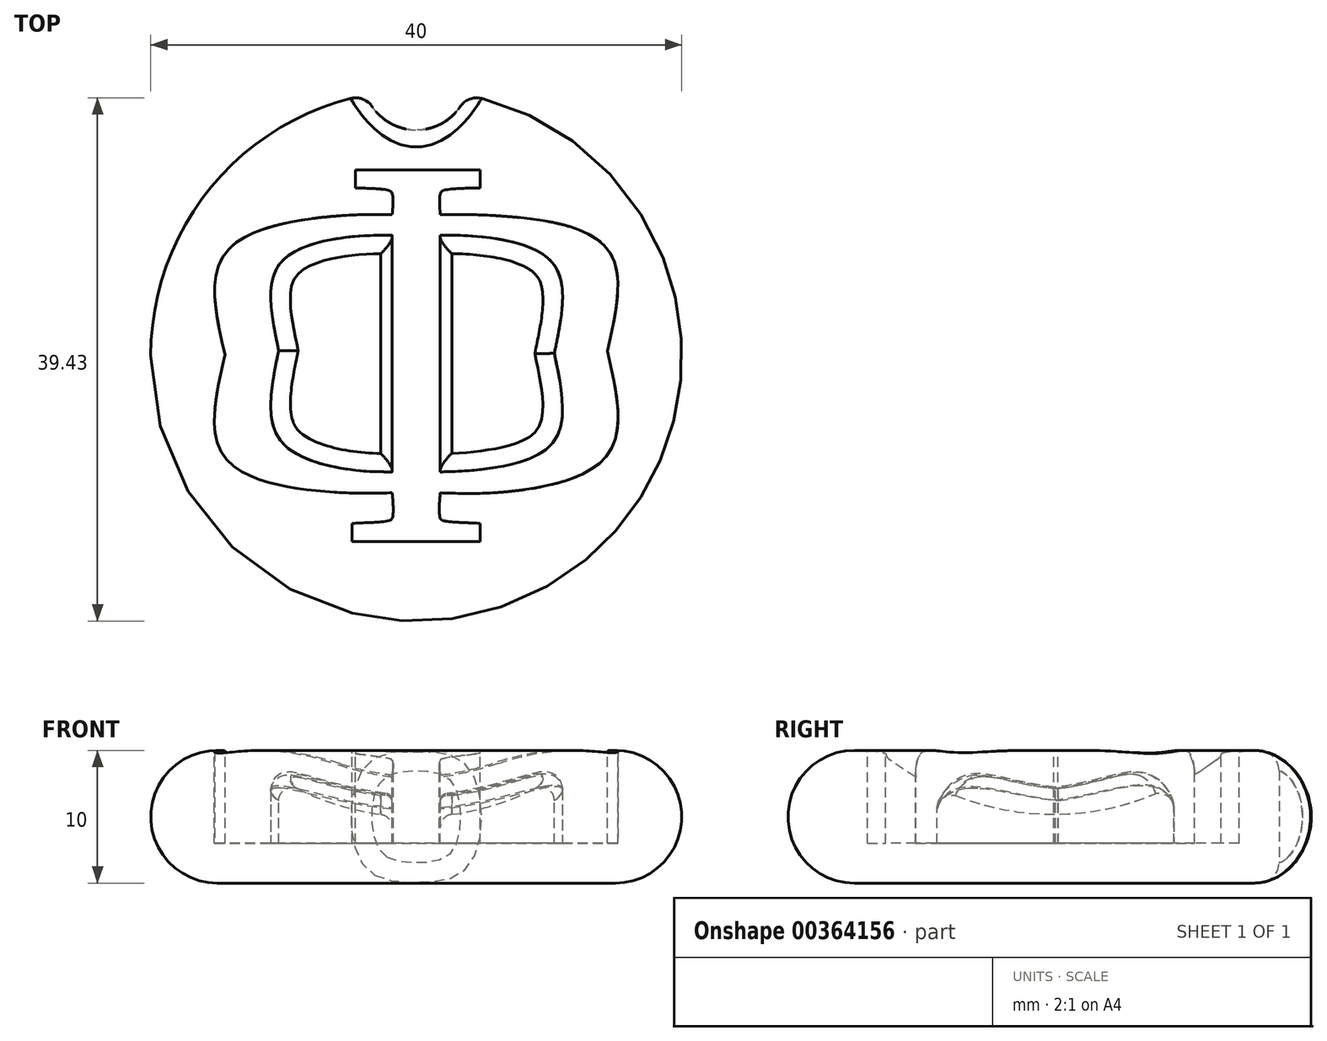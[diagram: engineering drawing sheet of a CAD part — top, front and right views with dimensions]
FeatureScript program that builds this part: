
annotation { "Feature Type Name" : "Feature", "Feature Type Description" : "" }
export const myFeature = defineFeature(function(context is Context, id is Id, definition is map)
    precondition{}
    {
        {
            var Q0;
            Q0=qCreatedBy(makeId("Right.planeOp"),FACE);
            var sketch = newSketch(context, id + "F0", { "sketchPlane" : qUnion([Q0])});
            skArc(sketch, "E0", {"start": v(-12, 9) * mm, "mid": v(-19.74, 6.58) * mm, "end": v(-15, 0) * mm});
            skArc(sketch, "E1", {"start": v(-12, 9) * mm, "mid": v(-6.32, 6.03) * mm, "end": v(0, 5) * mm});
            skLineSegment(sketch, "E2", {"start": v(-15, 0) * mm, "end": v(0, 0) * mm});
            skLineSegment(sketch, "E3", {"start": v(0, 0) * mm, "end": v(0, 5) * mm});
            skSolve(sketch);
        }
        {
            var Q0;
            Q0=makeQuery(id+"F0.imprint","IMPRINT",FACE,{"disambiguationData":[TD([[makeQuery(id+"F0.imprint","IMPRINT",EDGE,{"derivedFrom":sQuery(id+"F0.wireOp",EDGE,"E0")}),1.0]])]});
            var Q1;
            Q1=sQuery(id+"F0.wireOp",EDGE,"E3");
            revolve(context, id + "F1", {"entities" : qUnion([Q0]), "axis" : qUnion([Q1]), "revolveType" : RevolveType.FULL});
        }
        {
            var Q0;
            Q0=qCreatedBy(makeId("Top.planeOp"),FACE);
            cPlane(context, id + "F2", {"entities" : qUnion([Q0]), "cplaneType" : CPlaneType.OFFSET, "offset" : 25 * mm, "width" : 150 * mm, "height" : 150 * mm});
        }
        {
            var Q0;
            Q0=qCreatedBy(id+"F2.planeOp",FACE);
            var sketch = newSketch(context, id + "F3", { "sketchPlane" : qUnion([Q0])});
            skFitSpline(sketch, "E4", {"points": [v(4.83, 12.64) * mm, v(2.1, 12.47) * mm, v(1.8, 12.21) * mm, v(1.8, 10.64) * mm]});
            skFitSpline(sketch, "E5", {"points": [v(1.8, 10.64) * mm, v(7.04, 10.47) * mm, v(14.4, 8.04) * mm, v(14.4, 0.34) * mm]});
            skFitSpline(sketch, "E6", {"points": [v(14.4, 0.34) * mm, v(14.4, -7.49) * mm, v(6.87, -10.26) * mm, v(1.8, -10.34) * mm]});
            skFitSpline(sketch, "E7", {"points": [v(1.8, -10.34) * mm, v(1.8, -12.26) * mm, v(2.15, -12.47) * mm, v(4.83, -12.64) * mm]});
            skFitSpline(sketch, "E8", {"points": [v(-4.83, -12.64) * mm, v(-2.15, -12.47) * mm, v(-1.8, -12.26) * mm, v(-1.8, -10.34) * mm]});
            skFitSpline(sketch, "E9", {"points": [v(-1.8, -10.34) * mm, v(-6.74, -10.26) * mm, v(-14.4, -7.7) * mm, v(-14.4, 0.04) * mm]});
            skFitSpline(sketch, "E10", {"points": [v(-14.4, 0.04) * mm, v(-14.4, 7.7) * mm, v(-7, 10.43) * mm, v(-1.8, 10.64) * mm]});
            skFitSpline(sketch, "E11", {"points": [v(-1.8, 10.64) * mm, v(-1.8, 12.21) * mm, v(-2.15, 12.47) * mm, v(-4.57, 12.64) * mm]});
            skLineSegment(sketch, "E12", {"start": v(4.83, -12.64) * mm, "end": v(4.83, -14) * mm});
            skLineSegment(sketch, "E13", {"start": v(4.83, -14) * mm, "end": v(-4.83, -14) * mm});
            skLineSegment(sketch, "E14", {"start": v(-4.83, -14) * mm, "end": v(-4.83, -12.64) * mm});
            skLineSegment(sketch, "E15", {"start": v(-4.83, -12.64) * mm, "end": v(4.83, -12.64) * mm});
            skFitSpline(sketch, "E16", {"points": [v(-1.8, 9.06) * mm, v(-5.43, 8.9) * mm, v(-10.36, 6.8) * mm, v(-10.36, 0.38) * mm]});
            skFitSpline(sketch, "E17", {"points": [v(-10.36, 0.38) * mm, v(-10.36, -6.21) * mm, v(-5.51, -8.51) * mm, v(-1.8, -8.77) * mm]});
            skLineSegment(sketch, "E18", {"start": v(-4.57, 12.64) * mm, "end": v(-4.57, 14) * mm});
            skLineSegment(sketch, "E19", {"start": v(-4.57, 14) * mm, "end": v(4.83, 14) * mm});
            skLineSegment(sketch, "E20", {"start": v(4.83, 14) * mm, "end": v(4.83, 12.64) * mm});
            skLineSegment(sketch, "E21", {"start": v(4.83, 12.64) * mm, "end": v(-4.57, 12.64) * mm});
            skFitSpline(sketch, "E22", {"points": [v(1.8, -8.77) * mm, v(5.43, -8.51) * mm, v(10.4, -6.43) * mm, v(10.4, 0.17) * mm]});
            skFitSpline(sketch, "E23", {"points": [v(10.4, 0.17) * mm, v(10.4, 6.8) * mm, v(5.43, 8.9) * mm, v(1.8, 9.06) * mm]});
            skLineSegment(sketch, "E24", {"start": v(-1.8, -8.77) * mm, "end": v(-1.8, 9.06) * mm});
            skLineSegment(sketch, "E25", {"start": v(-1.8, 9.06) * mm, "end": v(-1.8, -8.77) * mm});
            skLineSegment(sketch, "E26", {"start": v(1.8, 9.06) * mm, "end": v(1.8, -8.77) * mm});
            skLineSegment(sketch, "E27", {"start": v(1.8, -8.77) * mm, "end": v(1.8, 9.06) * mm});
            skSolve(sketch);
        }
        {
            var Q0;
            Q0 = qSketchRegion(id + "F3", true);
            extrude(context, id + "F4", {"entities" : qUnion([Q0]), "operationType" : NewBodyOperationType.REMOVE, "oppositeDirection" : true, "depth" : 22 * mm});
        }
        {
            var Q0;
            Q0=qCreatedBy(makeId("Top.planeOp"),FACE);
            var sketch = newSketch(context, id + "F5", { "sketchPlane" : qUnion([Q0])});
            skCircle(sketch, "E28", {"center": v(0, 21) * mm, "radius": 4 * mm});
            skSolve(sketch);
        }
        {
            var Q0;
            Q0 = qSketchRegion(id + "F5", true);
            extrude(context, id + "F6", {"entities" : qUnion([Q0]), "operationType" : NewBodyOperationType.REMOVE, "depth" : 25 * mm});
        }
        {
            var Q0;
            Q0=makeQuery(id+"F6.boolean.opBoolean","INTERSECT",EDGE,{"derivedFrom":[makeQuery(id+"F1.opRevolve","SWEPT_FACE",FACE,{"disambiguationData":[OSD([sQuery(id+"F0.wireOp",EDGE,"E0")])]}),makeQuery(id+"F6.opExtrude","SWEPT_FACE",FACE,{"disambiguationData":[OSD([sQuery(id+"F5.wireOp",EDGE,"E28")])]})]});
            fillet(context, id + "F7", {"entities" : qUnion([Q0]), "radius" : 1.5 * mm, "tangentPropagation" : true, "allowEdgeOverflow" : false});
        }
        {
            var Q0;
            Q0=makeQuery(id+"F4.boolean.opBoolean","SPLIT",FACE,{"disambiguationData":[TD([makeQuery(id+"F4.opExtrude","SWEPT_FACE",FACE,{"disambiguationData":[OSD([sQuery(id+"F3.wireOp",EDGE,"E22")])]})])],"derivedFrom":makeQuery(id+"F1.opRevolve","SWEPT_FACE",FACE,{"disambiguationData":[OSD([sQuery(id+"F0.wireOp",EDGE,"E1")])]})});
            fillet(context, id + "F8", {"entities" : qUnion([Q0]), "radius" : 1 * mm, "tangentPropagation" : true, "allowEdgeOverflow" : false});
        }
        {
            var Q0;
            Q0=makeQuery(id+"F4.boolean.opBoolean","SPLIT",FACE,{"disambiguationData":[TD([makeQuery(id+"F4.opExtrude","SWEPT_FACE",FACE,{"disambiguationData":[OSD([sQuery(id+"F3.wireOp",EDGE,"E16")])]})])],"derivedFrom":makeQuery(id+"F1.opRevolve","SWEPT_FACE",FACE,{"disambiguationData":[OSD([sQuery(id+"F0.wireOp",EDGE,"E1")])]})});
            fillet(context, id + "F9", {"entities" : qUnion([Q0]), "radius" : 1 * mm, "tangentPropagation" : true, "allowEdgeOverflow" : false});
        }
    });
